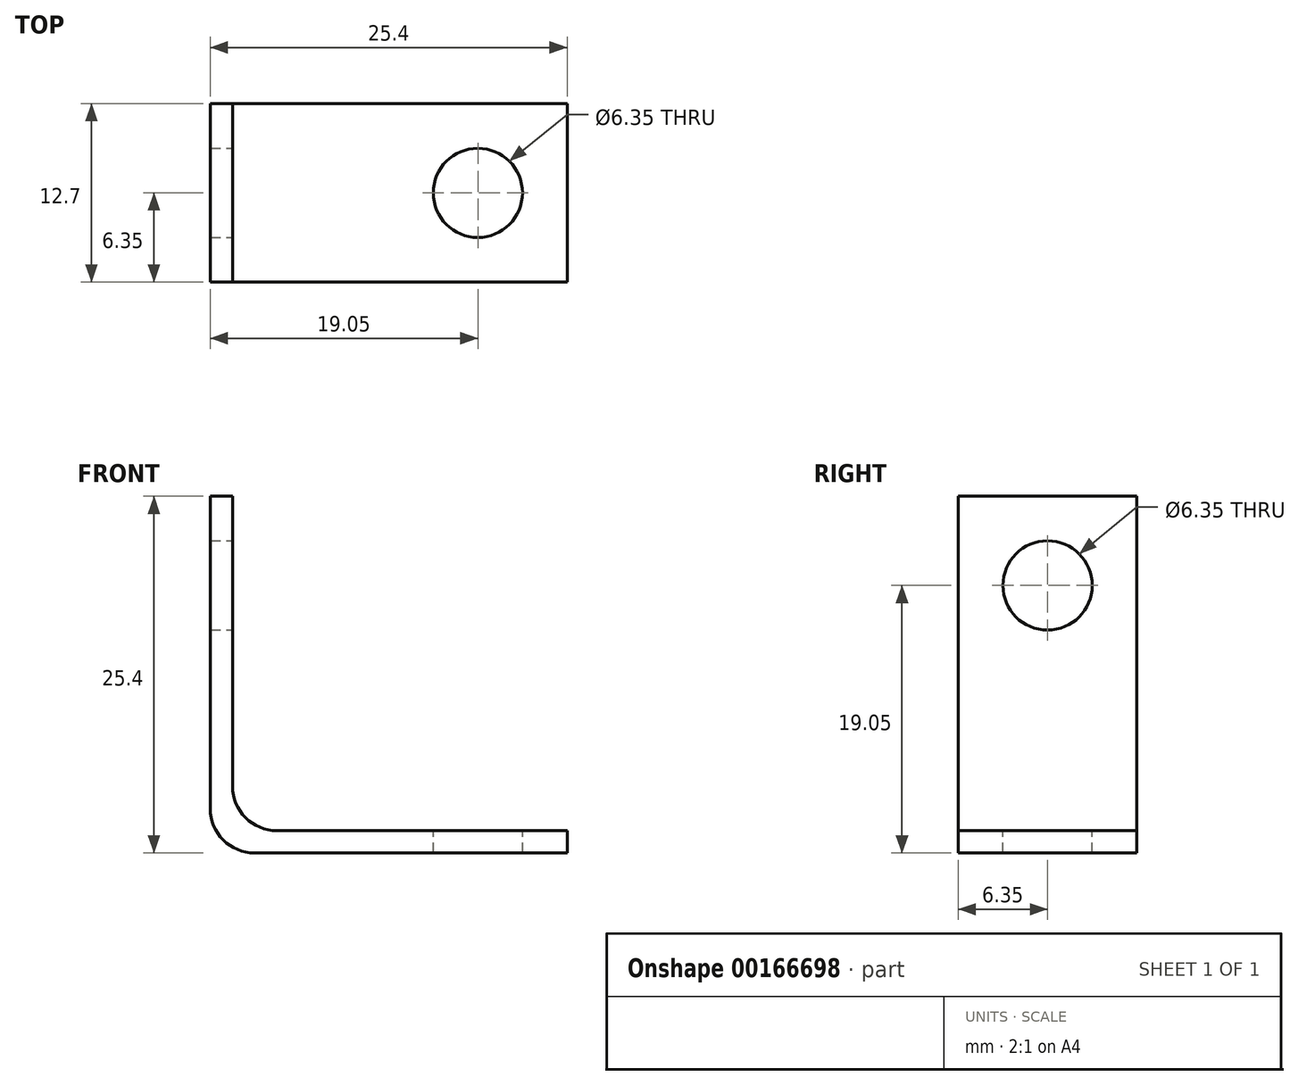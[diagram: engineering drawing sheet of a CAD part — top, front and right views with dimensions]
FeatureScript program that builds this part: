
annotation { "Feature Type Name" : "Feature", "Feature Type Description" : "" }
export const myFeature = defineFeature(function(context is Context, id is Id, definition is map)
    precondition{}
    {
        {
            var Q0;
            Q0=qCreatedBy(makeId("Front.planeOp"),FACE);
            var sketch = newSketch(context, id + "F0", { "sketchPlane" : qUnion([Q0])});
            skLineSegment(sketch, "E0", {"start": v(0, 3.18) * mm, "end": v(0, 25.4) * mm});
            skLineSegment(sketch, "E1", {"start": v(3.18, 0) * mm, "end": v(25.4, 0) * mm});
            skLineSegment(sketch, "E2.0", {"start": v(1.59, 4.76) * mm, "end": v(1.59, 25.4) * mm});
            skLineSegment(sketch, "E2.1", {"start": v(4.76, 1.59) * mm, "end": v(25.4, 1.59) * mm});
            skLineSegment(sketch, "E3", {"start": v(0, 25.4) * mm, "end": v(1.59, 25.4) * mm});
            skLineSegment(sketch, "E4", {"start": v(25.4, 1.59) * mm, "end": v(25.4, 0) * mm});
            skPoint(sketch, "E5.visualSharp", {"position": v(1.59, 1.59) * mm});
            skArc(sketch, "E5.filletArc", {"start": v(1.59, 4.76) * mm, "mid": v(2.52, 2.52) * mm, "end": v(4.76, 1.59) * mm});
            skPoint(sketch, "E6.visualSharp", {"position": v(0, 0) * mm});
            skArc(sketch, "E6.filletArc", {"start": v(0, 3.18) * mm, "mid": v(0.93, 0.93) * mm, "end": v(3.18, 0) * mm});
            skSolve(sketch);
        }
        {
            var Q0;
            Q0=makeQuery(id+"F0.imprint","IMPRINT",FACE,{"disambiguationData":[TD([[makeQuery(id+"F0.imprint","IMPRINT",EDGE,{"derivedFrom":sQuery(id+"F0.wireOp",EDGE,"E0")}),-1.0]])]});
            extrude(context, id + "F1", {"entities" : qUnion([Q0]), "depth" : 6.35 * mm, "hasSecondDirection" : true, "secondDirectionOppositeDirection" : true, "secondDirectionDepth" : 6.35 * mm});
        }
        {
            var Q0;
            Q0=makeQuery(id+"F1.opExtrude","SWEPT_FACE",FACE,{"disambiguationData":[OSD([sQuery(id+"F0.wireOp",EDGE,"E2.1")])]});
            var sketch = newSketch(context, id + "F2", { "sketchPlane" : qUnion([Q0])});
            skCircle(sketch, "E7", {"center": v(19.05, 0) * mm, "radius": 3.18 * mm});
            skSolve(sketch);
        }
        {
            var Q0;
            Q0=makeQuery(id+"F1.opExtrude","SWEPT_FACE",FACE,{"disambiguationData":[OSD([sQuery(id+"F0.wireOp",EDGE,"E2.0")])]});
            var sketch = newSketch(context, id + "F3", { "sketchPlane" : qUnion([Q0])});
            skCircle(sketch, "E8", {"center": v(0, 19.05) * mm, "radius": 3.18 * mm});
            skSolve(sketch);
        }
        {
            var Q0;
            Q0=makeQuery(id+"F3.imprint","IMPRINT",FACE,{"disambiguationData":[TD([[makeQuery(id+"F3.imprint","IMPRINT",EDGE,{"derivedFrom":sQuery(id+"F3.wireOp",EDGE,"E8")}),1.0]])]});
            extrude(context, id + "F4", {"entities" : qUnion([Q0]), "operationType" : NewBodyOperationType.REMOVE, "endBound" : BoundingType.THROUGH_ALL, "oppositeDirection" : true, "depth" : 25.4 * mm});
        }
        {
            var Q0;
            Q0=makeQuery(id+"F2.imprint","IMPRINT",FACE,{"disambiguationData":[TD([[makeQuery(id+"F2.imprint","IMPRINT",EDGE,{"derivedFrom":sQuery(id+"F2.wireOp",EDGE,"E7")}),1.0]])]});
            extrude(context, id + "F5", {"entities" : qUnion([Q0]), "operationType" : NewBodyOperationType.REMOVE, "endBound" : BoundingType.THROUGH_ALL, "oppositeDirection" : true, "depth" : 25.4 * mm});
        }
    });
